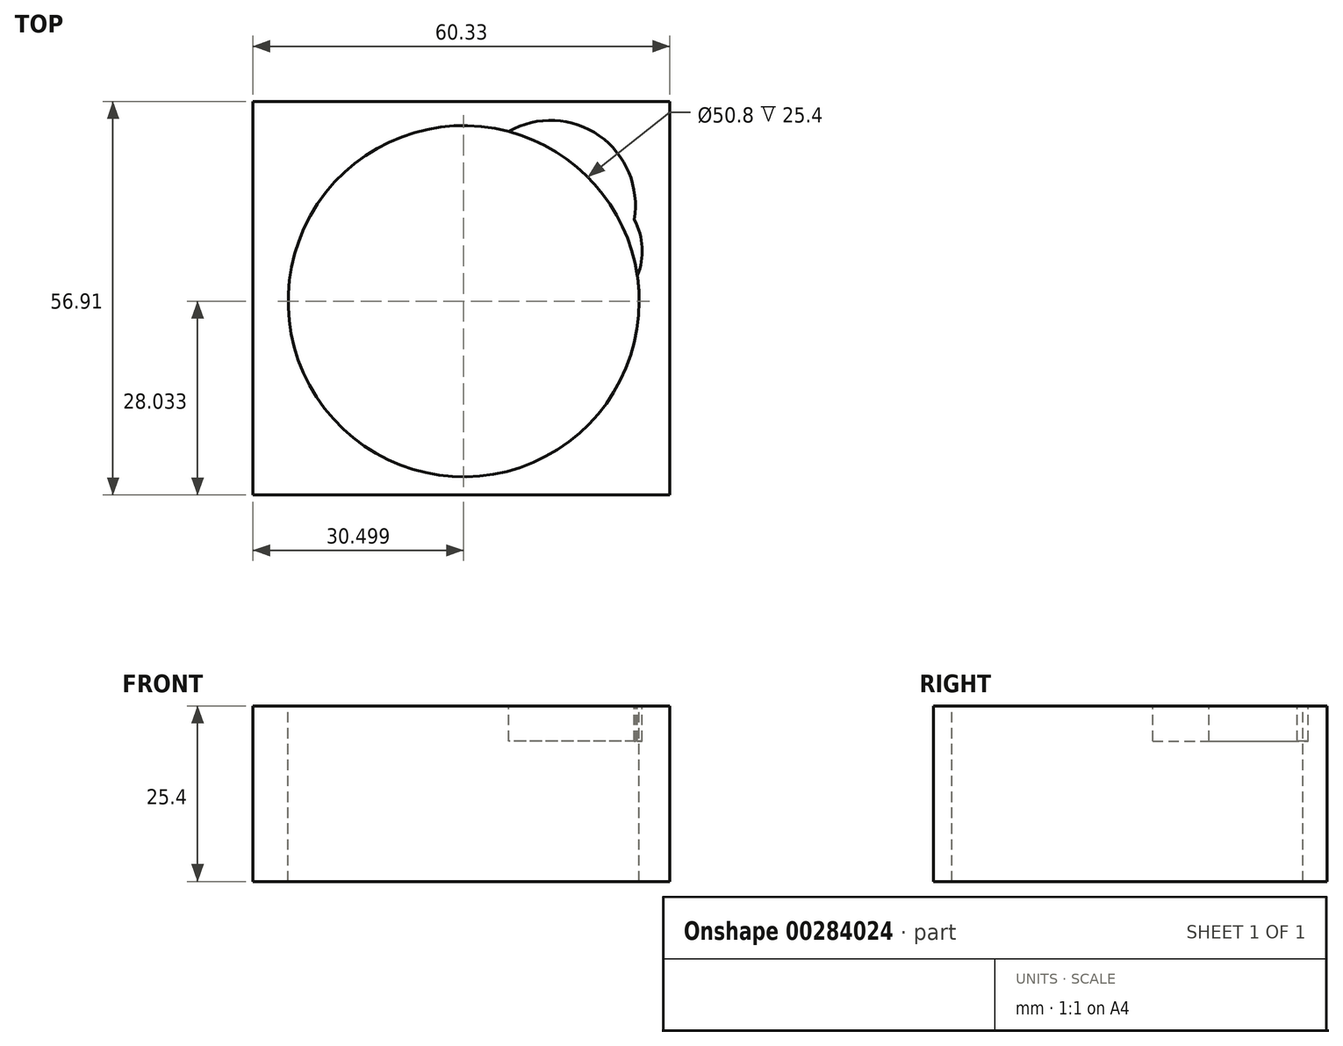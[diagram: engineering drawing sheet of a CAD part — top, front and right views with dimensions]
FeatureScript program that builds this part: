
annotation { "Feature Type Name" : "Feature", "Feature Type Description" : "" }
export const myFeature = defineFeature(function(context is Context, id is Id, definition is map)
    precondition{}
    {
        {
            var Q0;
            Q0=qCreatedBy(makeId("Top.planeOp"),FACE);
            var sketch = newSketch(context, id + "F0", { "sketchPlane" : qUnion([Q0])});
            skLineSegment(sketch, "E0.bottom", {"start": v(0, 0) * mm, "end": v(60.33, 0) * mm});
            skLineSegment(sketch, "E0.top", {"start": v(0, 56.9) * mm, "end": v(60.33, 56.9) * mm});
            skLineSegment(sketch, "E0.left", {"start": v(0, 0) * mm, "end": v(0, 56.9) * mm});
            skLineSegment(sketch, "E0.right", {"start": v(60.33, 0) * mm, "end": v(60.33, 56.9) * mm});
            skSolve(sketch);
        }
        {
            var Q0;
            Q0=makeQuery(id+"F0.imprint","IMPRINT",FACE,{"disambiguationData":[TD([[makeQuery(id+"F0.imprint","IMPRINT",EDGE,{"derivedFrom":sQuery(id+"F0.wireOp",EDGE,"E0.bottom")}),1.0]])]});
            extrude(context, id + "F1", {"entities" : qUnion([Q0]), "depth" : 25.4 * mm});
        }
        {
            var Q0;
            Q0=makeQuery(id+"F1.opExtrude","CAP_FACE",FACE,{"disambiguationData":[OSD([sQuery(id+"F0.wireOp",EDGE,"E0.bottom"),sQuery(id+"F0.wireOp",EDGE,"E0.top"),sQuery(id+"F0.wireOp",EDGE,"E0.left"),sQuery(id+"F0.wireOp",EDGE,"E0.right")])],"isStart":false});
            var sketch = newSketch(context, id + "F2", { "sketchPlane" : qUnion([Q0])});
            skCircle(sketch, "E1", {"center": v(43.07, 41.9) * mm, "radius": 12.28 * mm});
            skCircle(sketch, "E2", {"center": v(46.72, 35.29) * mm, "radius": 9.6 * mm});
            skSolve(sketch);
        }
        {
            var Q0;
            {var subQ0=sQuery(id+"F2.wireOp",EDGE,"E2");var subQ1=sQuery(id+"F2.wireOp",EDGE,"E1");var subQ2=makeQuery(id+"F2.imprint","INTERSECT",VERTEX,{"disambiguationData":[OD(0.0)],"derivedFrom":[subQ1,subQ0]});Q0=makeQuery(id+"F2.imprint","IMPRINT",FACE,{"disambiguationData":[TD([[makeQuery(id+"F2.imprint","IMPRINT",EDGE,{"disambiguationData":[TD([[subQ2,1.0]])],"derivedFrom":subQ1}),1.0]])]});}
            var Q1;
            {var subQ0=sQuery(id+"F2.wireOp",EDGE,"E2");var subQ1=sQuery(id+"F2.wireOp",EDGE,"E1");var subQ2=makeQuery(id+"F2.imprint","INTERSECT",VERTEX,{"disambiguationData":[OD(0.0)],"derivedFrom":[subQ1,subQ0]});Q1=makeQuery(id+"F2.imprint","IMPRINT",FACE,{"disambiguationData":[TD([[makeQuery(id+"F2.imprint","IMPRINT",EDGE,{"disambiguationData":[TD([[subQ2,-1.0]])],"derivedFrom":subQ1}),1.0]])]});}
            var Q2;
            {var subQ0=sQuery(id+"F2.wireOp",EDGE,"E2");var subQ1=sQuery(id+"F2.wireOp",EDGE,"E1");var subQ2=makeQuery(id+"F2.imprint","INTERSECT",VERTEX,{"disambiguationData":[OD(0.0)],"derivedFrom":[subQ1,subQ0]});Q2=makeQuery(id+"F2.imprint","IMPRINT",FACE,{"disambiguationData":[TD([[makeQuery(id+"F2.imprint","IMPRINT",EDGE,{"disambiguationData":[TD([[subQ2,-1.0]])],"derivedFrom":subQ1}),-1.0]])]});}
            extrude(context, id + "F3", {"entities" : qUnion([Q0, Q1, Q2]), "operationType" : NewBodyOperationType.REMOVE, "oppositeDirection" : true, "depth" : 5.08 * mm});
        }
        {
            var Q0;
            Q0=makeQuery(id+"F1.opExtrude","CAP_FACE",FACE,{"disambiguationData":[OSD([sQuery(id+"F0.wireOp",EDGE,"E0.bottom"),sQuery(id+"F0.wireOp",EDGE,"E0.top"),sQuery(id+"F0.wireOp",EDGE,"E0.left"),sQuery(id+"F0.wireOp",EDGE,"E0.right")])],"isStart":false});
            var sketch = newSketch(context, id + "F4", { "sketchPlane" : qUnion([Q0])});
            skCircle(sketch, "E3", {"center": v(30.5, 28.03) * mm, "radius": 25.4 * mm});
            skSolve(sketch);
        }
        {
            var Q0;
            {var subQ0=sQuery(id+"F4.wireOp",EDGE,"E3");var subQ1=makeQuery(id+"F3.boolean.opBoolean","COPY",EDGE,{"derivedFrom":makeQuery(id+"F3.opExtrude","CAP_EDGE",EDGE,{"disambiguationData":[OSD([sQuery(id+"F2.wireOp",EDGE,"E1")])],"isStart":true})});var subQ2=makeQuery(id+"F4.imprint","INTERSECT",VERTEX,{"derivedFrom":[subQ1,subQ0]});Q0=makeQuery(id+"F4.imprint","IMPRINT",FACE,{"disambiguationData":[TD([[makeQuery(id+"F4.imprint","IMPRINT",EDGE,{"disambiguationData":[TD([[subQ2,-1.0]])],"derivedFrom":subQ0}),1.0]])]});}
            var Q1;
            {var subQ0=sQuery(id+"F4.wireOp",EDGE,"E3");var subQ1=makeQuery(id+"F3.boolean.opBoolean","COPY",EDGE,{"derivedFrom":makeQuery(id+"F3.opExtrude","CAP_EDGE",EDGE,{"disambiguationData":[OSD([sQuery(id+"F2.wireOp",EDGE,"E1")])],"isStart":true})});var subQ2=makeQuery(id+"F4.imprint","INTERSECT",VERTEX,{"derivedFrom":[subQ1,subQ0]});Q1=makeQuery(id+"F4.imprint","IMPRINT",FACE,{"disambiguationData":[TD([[makeQuery(id+"F4.imprint","IMPRINT",EDGE,{"disambiguationData":[TD([[subQ2,1.0]])],"derivedFrom":subQ0}),1.0]])]});}
            extrude(context, id + "F5", {"entities" : qUnion([Q0, Q1]), "operationType" : NewBodyOperationType.REMOVE, "endBound" : BoundingType.THROUGH_ALL, "oppositeDirection" : true, "depth" : 25.4 * mm});
        }
    });
